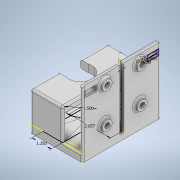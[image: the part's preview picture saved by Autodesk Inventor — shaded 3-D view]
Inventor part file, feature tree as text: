
AUTODESK INVENTOR PART (.ipt)
format: ipt  version: 2020 (Build 240168000, 168)  size: 449,536 bytes
history: native  units: in
note: dims shown in document units (in); Inventor stores cm internally (conversion verified against a paired STEP export)
features: sketch x16, extrude x13, hole x4, plane x1, mirror x1, fillet x1
ambient origin geometry x8: Origin, YZ Plane, XZ Plane, XY Plane, X Axis, Y Axis, Z Axis, Center Point
bodies: Solid1 (feature_tree)
feature tree (36):
  extrude  "Extrusion1"  Depth=5.0299in
  extrude  "Extrusion2"  Depth=0.375in
  extrude  "Extrusion3"  Depth=2.8543in
  sketch  "Sketch5"  dims[d24=5.315in d25=4.5472in]
  extrude  "Extrusion4"  Depth=4.5472in
  extrude  "Extrusion5"  Depth=0.25in
  extrude  "Extrusion6"  Depth=2.6575in
  hole  "Hole2"  [1 undecoded]
  extrude  "Extrusion7"  Depth=0.5in
  extrude  "Extrusion8"  Depth=5.03in
  extrude  "Extrusion9"  Depth=0.5in
  extrude  "Extrusion10"  Depth=0.5in
  hole  "Hole3"  [1 undecoded]
  extrude  "Extrusion11"  Depth=1.5in TaperAngle=0.0deg
  extrude  "Extrusion12"  Depth=1.125in
  hole  "Hole4"  [1 undecoded]
  sketch  "Sketch17"  dims[d63=2.25in d64=90.0deg d65=2.25in d66=90.0deg d67=0.332in d68=0.375in d69=0.119in d70=0.25in d71=0.5635in d72=0.375in d73=0.0in d74=0.0in d75=0.0in d76=0.625in d77=0.625in d78=0.625in d79=0.625in d80=0.2in d81=0.0in d82=0.21in d83=1.125in d84=0.185in d85=0.37in d86=0.09in d87=0.375in d88=0.119in d89=0.25in d90=0.5635in d91=0.375in d92=0.0in d93=0.375in d94=0.0in d95=0.25in d96=0.5in d97=0.375in d98=0.125in d99=0.0in d100=0.129in d101=0.198in d102=0.225in d103=0.188in d104=0.5635in d105=0.375in d106=0.0in d107=0.125in d108=0.125in]
  extrude  "Extrusion13"  TaperAngle=90.0deg  [1 undecoded]
  hole  "Hole5"  [1 undecoded]
  plane  "Work Plane1"
  mirror  "Mirror1"
  fillet  "Fillet1"  [1 undecoded]
  sketch  "Sketch1"  dims[d0=3.3654in d1=5.0299in]
  sketch  "Sketch3"  dims[d3=45.0deg d4=0.375in]
  sketch  "Sketch4"  dims[d5=0.5in d6=0.0in d23=2.8543in]
  sketch  "Sketch6"  dims[d26=0.1in d27=0.0in d28=0.25in]
  sketch  "Sketch7"  dims[d29=0.1in d30=0.0in d31=2.6575in]
  sketch  "Sketch8"  dims[d32=1.5in d33=1.25in]
  sketch  "Sketch9"  dims[d34=1.9685in d35=0.0in d36=0.5in]
  sketch  "Sketch10"  dims[d37=5.03in d38=0.0in d39=1.5in]
  sketch  "Sketch11"  dims[d40=1.0in d41=0.0in d42=0.5in]
  sketch  "Sketch12"  dims[d43=0.0in d44=0.5in]
  sketch  "Sketch13"  dims[d45=0.201in d46=0.75in d47=0.385in d48=0.25in d49=0.5635in d50=1.378in d51=0.0in d52=1.9685in d53=0.0in]
  sketch  "Sketch14"  dims[d54=1.9685in d55=0.0in d56=1.5in d57=0.0in]
  sketch  "Sketch15"  dims[d58=3.75in d59=0.0in d60=1.125in]
  sketch  "Sketch16"  dims[d61=1.49in d62=2.25in]
note: 6 required parameter values undecoded (feature->parameter linkage not recoverable at this tier; creation-order binding heuristic only, values carry confidence <= 0.55)
